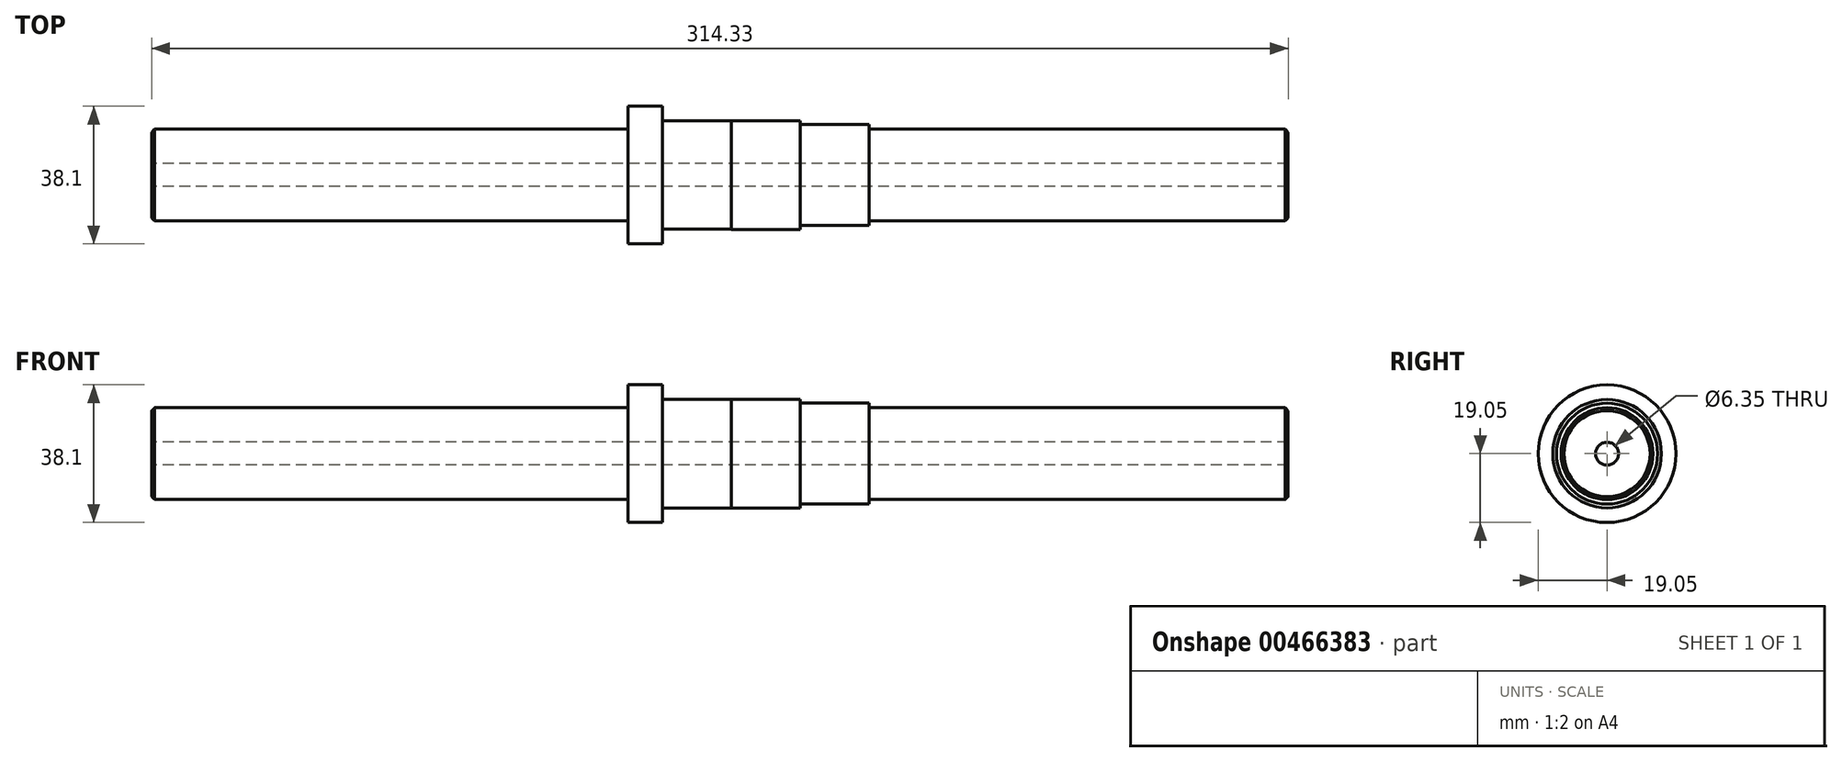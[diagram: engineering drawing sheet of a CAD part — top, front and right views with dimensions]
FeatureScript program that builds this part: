
annotation { "Feature Type Name" : "Feature", "Feature Type Description" : "" }
export const myFeature = defineFeature(function(context is Context, id is Id, definition is map)
    precondition{}
    {
        {
            var Q0;
            Q0=qCreatedBy(makeId("Front.planeOp"),FACE);
            var sketch = newSketch(context, id + "F0", { "sketchPlane" : qUnion([Q0])});
            skLineSegment(sketch, "E0", {"start": v(0, 0) * mm, "end": v(314.33, 0) * mm});
            skLineSegment(sketch, "E1", {"start": v(0, 0) * mm, "end": v(0, 12.7) * mm});
            skLineSegment(sketch, "E2", {"start": v(0, 12.7) * mm, "end": v(131.76, 12.7) * mm});
            skLineSegment(sketch, "E3", {"start": v(131.76, 12.7) * mm, "end": v(131.76, 19.05) * mm});
            skLineSegment(sketch, "E4", {"start": v(131.76, 19.05) * mm, "end": v(141.29, 19.05) * mm});
            skLineSegment(sketch, "E5", {"start": v(141.29, 19.05) * mm, "end": v(141.29, 15) * mm});
            skLineSegment(sketch, "E6", {"start": v(141.29, 15) * mm, "end": v(160.34, 15) * mm});
            skLineSegment(sketch, "E7", {"start": v(160.34, 15.01) * mm, "end": v(160.34, 15) * mm});
            skLineSegment(sketch, "E8", {"start": v(160.34, 15.01) * mm, "end": v(179.39, 15.01) * mm});
            skLineSegment(sketch, "E9", {"start": v(179.39, 15.01) * mm, "end": v(179.39, 13.97) * mm});
            skLineSegment(sketch, "E10", {"start": v(179.39, 13.97) * mm, "end": v(198.44, 13.97) * mm});
            skLineSegment(sketch, "E11", {"start": v(198.44, 13.97) * mm, "end": v(198.44, 12.7) * mm});
            skPoint(sketch, "E12.orphan", {"position": v(171.27, 0) * mm});
            skLineSegment(sketch, "E13", {"start": v(198.44, 12.7) * mm, "end": v(314.33, 12.7) * mm});
            skLineSegment(sketch, "E14", {"start": v(314.33, 12.7) * mm, "end": v(314.33, 0) * mm});
            skSolve(sketch);
        }
        {
            var Q0;
            Q0 = qSketchRegion(id + "F0", true);
            var Q1;
            Q1=sQuery(id+"F0.wireOp",EDGE,"E0");
            revolve(context, id + "F1", {"entities" : qUnion([Q0]), "axis" : qUnion([Q1]), "revolveType" : RevolveType.FULL});
        }
        {
            var Q0;
            Q0=makeQuery(id+"F1.opRevolve","SWEPT_FACE",FACE,{"disambiguationData":[OSD([sQuery(id+"F0.wireOp",EDGE,"E1")])]});
            var sketch = newSketch(context, id + "F2", { "sketchPlane" : qUnion([Q0])});
            skCircle(sketch, "E15", {"center": v(0, 0) * mm, "radius": 3.18 * mm});
            skSolve(sketch);
        }
        {
            var Q0;
            Q0 = qSketchRegion(id + "F2", true);
            extrude(context, id + "F3", {"entities" : qUnion([Q0]), "operationType" : NewBodyOperationType.REMOVE, "endBound" : BoundingType.THROUGH_ALL, "oppositeDirection" : true, "depth" : 25.4 * mm});
        }
        {
            var Q0;
            Q0=makeQuery(id+"F1.opRevolve","SWEPT_EDGE",EDGE,{"disambiguationData":[OSD([sQuery(id+"F0.wireOp",EDGE,"E1"),sQuery(id+"F0.wireOp",EDGE,"E2")])]});
            var Q1;
            Q1=makeQuery(id+"F1.opRevolve","SWEPT_EDGE",EDGE,{"disambiguationData":[OSD([sQuery(id+"F0.wireOp",EDGE,"E13"),sQuery(id+"F0.wireOp",EDGE,"E14")])]});
            chamfer(context, id + "F4", {"entities" : qUnion([Q0, Q1]), "width" : 0.8 * mm, "tangentPropagation" : true});
        }
    });
